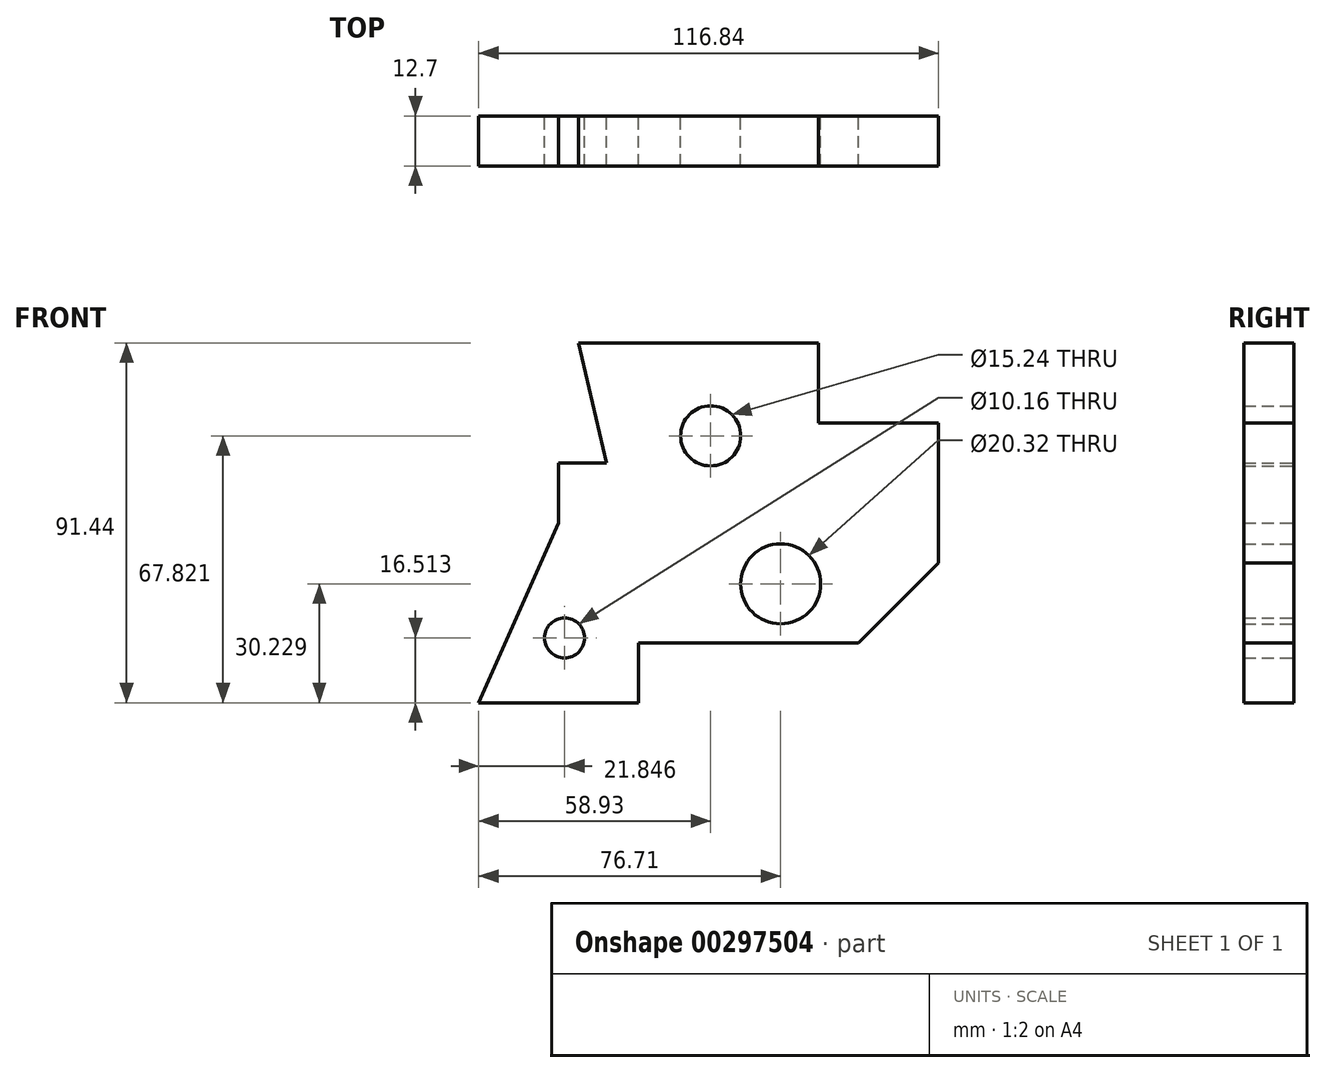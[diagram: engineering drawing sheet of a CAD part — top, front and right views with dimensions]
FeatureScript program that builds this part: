
annotation { "Feature Type Name" : "Feature", "Feature Type Description" : "" }
export const myFeature = defineFeature(function(context is Context, id is Id, definition is map)
    precondition{}
    {
        {
            var Q0;
            Q0=qCreatedBy(makeId("Front.planeOp"),FACE);
            var sketch = newSketch(context, id + "F0", { "sketchPlane" : qUnion([Q0])});
            skLineSegment(sketch, "E0", {"start": v(-33.53, 34.1) * mm, "end": v(27.43, 34.1) * mm});
            skLineSegment(sketch, "E1", {"start": v(27.43, 34.1) * mm, "end": v(27.43, 13.78) * mm});
            skLineSegment(sketch, "E2", {"start": v(27.43, 13.78) * mm, "end": v(57.91, 13.78) * mm});
            skLineSegment(sketch, "E3", {"start": v(57.91, 13.78) * mm, "end": v(57.91, -21.78) * mm});
            skLineSegment(sketch, "E4", {"start": v(57.91, -21.78) * mm, "end": v(37.6, -42.1) * mm});
            skLineSegment(sketch, "E5", {"start": v(37.6, -42.1) * mm, "end": v(-18.29, -42.1) * mm});
            skLineSegment(sketch, "E6", {"start": v(-18.29, -42.1) * mm, "end": v(-18.29, -57.34) * mm});
            skLineSegment(sketch, "E7", {"start": v(-18.29, -57.34) * mm, "end": v(-58.93, -57.34) * mm});
            skLineSegment(sketch, "E8", {"start": v(-38.6, 3.62) * mm, "end": v(-26.51, 3.62) * mm});
            skLineSegment(sketch, "E9", {"start": v(-26.51, 3.62) * mm, "end": v(-33.53, 34.1) * mm});
            skCircle(sketch, "E10", {"center": v(-37.08, -40.83) * mm, "radius": 5.08 * mm});
            skCircle(sketch, "E11", {"center": v(0, 10.48) * mm, "radius": 7.62 * mm});
            skCircle(sketch, "E12", {"center": v(17.78, -27.11) * mm, "radius": 10.16 * mm});
            skLineSegment(sketch, "E13", {"start": v(-38.6, 3.62) * mm, "end": v(-38.6, -11.62) * mm});
            skLineSegment(sketch, "E14", {"start": v(-38.6, -11.62) * mm, "end": v(-58.93, -57.34) * mm});
            skSolve(sketch);
        }
        {
            var Q0;
            Q0=makeQuery(id+"F0.imprint","IMPRINT",FACE,{"disambiguationData":[TD([[makeQuery(id+"F0.imprint","IMPRINT",EDGE,{"derivedFrom":sQuery(id+"F0.wireOp",EDGE,"E0")}),-1.0]])]});
            extrude(context, id + "F1", {"entities" : qUnion([Q0]), "depth" : 12.7 * mm});
        }
    });
